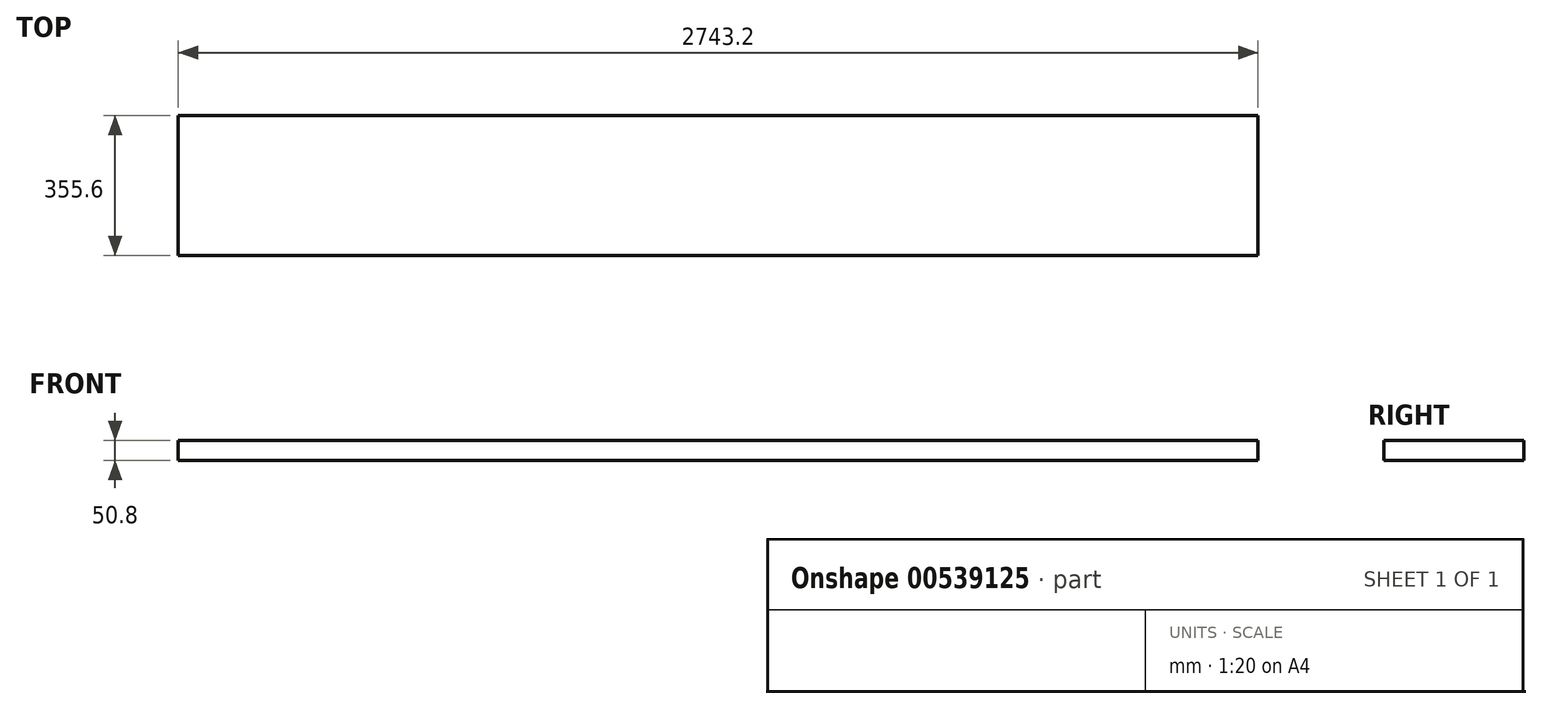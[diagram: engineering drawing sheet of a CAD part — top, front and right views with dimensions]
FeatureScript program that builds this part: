
annotation { "Feature Type Name" : "Feature", "Feature Type Description" : "" }
export const myFeature = defineFeature(function(context is Context, id is Id, definition is map)
    precondition{}
    {
        {
            var Q0;
            Q0=qCreatedBy(makeId("Top.planeOp"),FACE);
            cPlane(context, id + "F0", {"entities" : qUnion([Q0]), "cplaneType" : CPlaneType.OFFSET, "offset" : 457.2 * mm, "width" : 152.4 * mm, "height" : 152.4 * mm});
        }
        {
            var Q0;
            Q0=qCreatedBy(id+"F0.planeOp",FACE);
            var sketch = newSketch(context, id + "F1", { "sketchPlane" : qUnion([Q0])});
            skLineSegment(sketch, "E0.bottom", {"start": v(-945.66, -976.04) * mm, "end": v(1797.54, -976.04) * mm});
            skLineSegment(sketch, "E0.top", {"start": v(-945.66, -620.44) * mm, "end": v(1797.54, -620.44) * mm});
            skLineSegment(sketch, "E0.left", {"start": v(-945.66, -976.04) * mm, "end": v(-945.66, -620.44) * mm});
            skLineSegment(sketch, "E0.right", {"start": v(1797.54, -976.04) * mm, "end": v(1797.54, -620.44) * mm});
            skSolve(sketch);
        }
        {
            var Q0;
            Q0=makeQuery(id+"F1.imprint","IMPRINT",FACE,{"disambiguationData":[TD([[makeQuery(id+"F1.imprint","IMPRINT",EDGE,{"derivedFrom":sQuery(id+"F1.wireOp",EDGE,"E0.bottom")}),1.0]])]});
            extrude(context, id + "F2", {"entities" : qUnion([Q0]), "oppositeDirection" : true, "depth" : 50.8 * mm, "offsetDistance" : 25.4 * mm});
        }
    });
